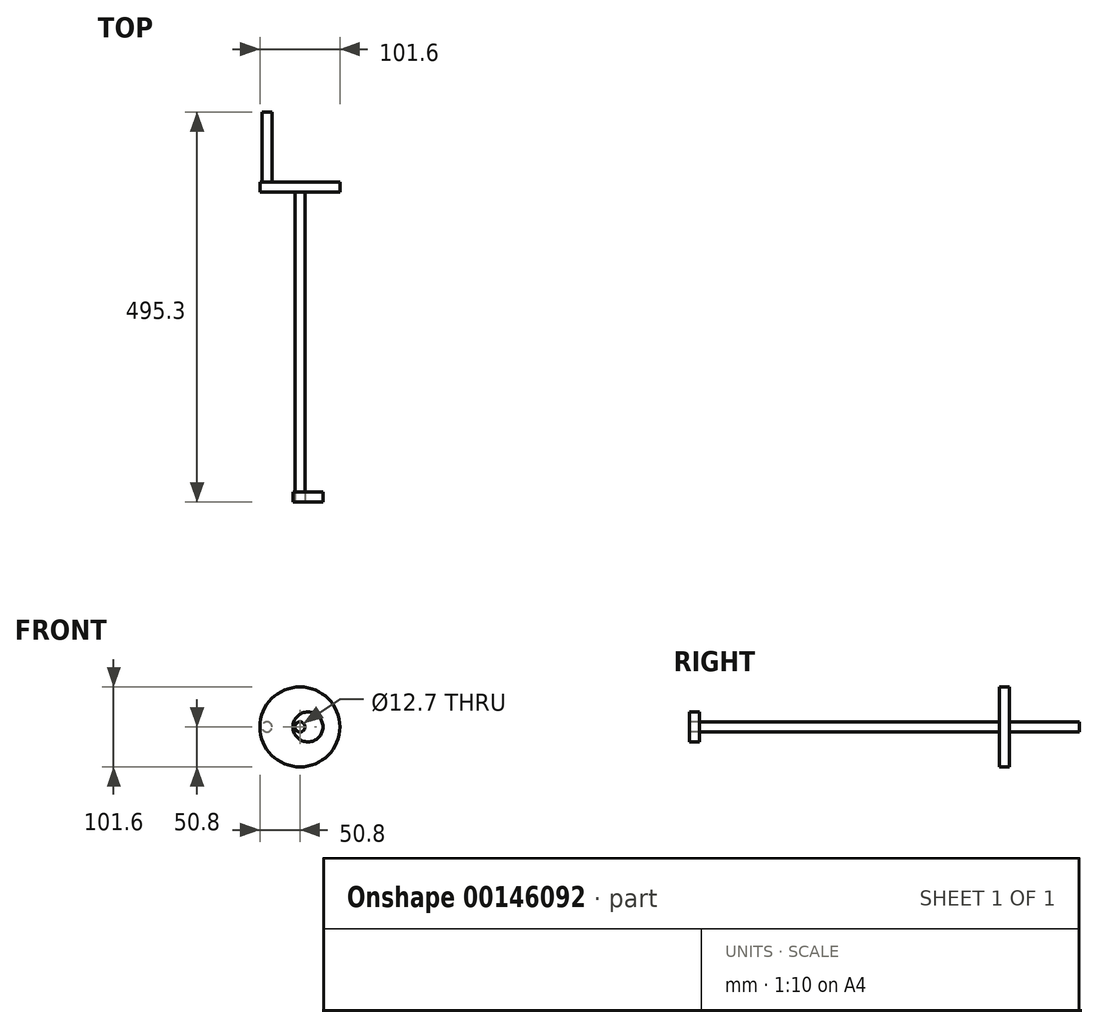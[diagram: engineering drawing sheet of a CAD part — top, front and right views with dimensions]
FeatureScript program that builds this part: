
annotation { "Feature Type Name" : "Feature", "Feature Type Description" : "" }
export const myFeature = defineFeature(function(context is Context, id is Id, definition is map)
    precondition{}
    {
        {
            var Q0;
            Q0=qCreatedBy(makeId("Front.planeOp"),FACE);
            var sketch = newSketch(context, id + "F0", { "sketchPlane" : qUnion([Q0])});
            skCircle(sketch, "E0", {"center": v(0, 0) * mm, "radius": 50.8 * mm});
            skCircle(sketch, "E1", {"center": v(0, 0) * mm, "radius": 6.35 * mm});
            skSolve(sketch);
        }
        {
            var Q0;
            Q0=makeQuery(id+"F0.imprint","IMPRINT",FACE,{"disambiguationData":[TD([[makeQuery(id+"F0.imprint","IMPRINT",EDGE,{"derivedFrom":sQuery(id+"F0.wireOp",EDGE,"E1")}),1.0]])]});
            extrude(context, id + "F1", {"entities" : qUnion([Q0]), "depth" : 393.7 * mm});
        }
        {
            var Q0;
            Q0=makeQuery(id+"F0.imprint","IMPRINT",FACE,{"disambiguationData":[TD([[makeQuery(id+"F0.imprint","IMPRINT",EDGE,{"derivedFrom":sQuery(id+"F0.wireOp",EDGE,"E0")}),1.0]])]});
            extrude(context, id + "F2", {"entities" : qUnion([Q0]), "operationType" : NewBodyOperationType.ADD, "depth" : 12.7 * mm});
        }
        {
            var Q0;
            Q0=makeQuery(id+"F0.imprint","IMPRINT",FACE,{"disambiguationData":[TD([[makeQuery(id+"F0.imprint","IMPRINT",EDGE,{"derivedFrom":sQuery(id+"F0.wireOp",EDGE,"E0")}),1.0]])]});
            var sketch = newSketch(context, id + "F3", { "sketchPlane" : qUnion([Q0])});
            skCircle(sketch, "E2", {"center": v(-41.91, 0) * mm, "radius": 6.35 * mm});
            skSolve(sketch);
        }
        {
            var Q0;
            Q0=makeQuery(id+"F3.imprint","IMPRINT",FACE,{"disambiguationData":[TD([[makeQuery(id+"F3.imprint","IMPRINT",EDGE,{"derivedFrom":sQuery(id+"F3.wireOp",EDGE,"E2")}),1.0]])]});
            extrude(context, id + "F4", {"entities" : qUnion([Q0]), "operationType" : NewBodyOperationType.ADD, "oppositeDirection" : true, "depth" : 88.9 * mm});
        }
        {
            var Q0;
            Q0=qCreatedBy(makeId("Right.planeOp"),FACE);
            var sketch = newSketch(context, id + "F5", { "sketchPlane" : qUnion([Q0])});
            skLineSegment(sketch, "E3", {"start": v(0, 0) * mm, "end": v(-393.7, 0) * mm});
            skLineSegment(sketch, "E4", {"start": v(0, 0) * mm, "end": v(-95.25, 0) * mm});
            skLineSegment(sketch, "E5", {"start": v(-95.25, 0) * mm, "end": v(-260.35, 0) * mm});
            skLineSegment(sketch, "E6", {"start": v(-260.35, 0) * mm, "end": v(-387.35, 0) * mm});
            skLineSegment(sketch, "E7", {"start": v(0, 0) * mm, "end": v(-12.7, 0) * mm});
            skLineSegment(sketch, "E8", {"start": v(-12.7, 0) * mm, "end": v(-19.05, 0) * mm});
            skLineSegment(sketch, "E9", {"start": v(-95.25, 0) * mm, "end": v(-107.95, 0) * mm});
            skLineSegment(sketch, "E10", {"start": v(-107.95, 0) * mm, "end": v(-114.3, 0) * mm});
            skLineSegment(sketch, "E11", {"start": v(-114.3, 0) * mm, "end": v(-127, 0) * mm});
            skLineSegment(sketch, "E12", {"start": v(-127, 0) * mm, "end": v(-133.35, 0) * mm});
            skLineSegment(sketch, "E13.2.0.0", {"start": v(-133.35, 0) * mm, "end": v(-146.05, 0) * mm});
            skLineSegment(sketch, "E13.3.0.0", {"start": v(-152.4, 0) * mm, "end": v(-165.1, 0) * mm});
            skLineSegment(sketch, "E13.4.0.0", {"start": v(-171.45, 0) * mm, "end": v(-184.15, 0) * mm});
            skLineSegment(sketch, "E13.5.0.0", {"start": v(-190.5, 0) * mm, "end": v(-203.2, 0) * mm});
            skLineSegment(sketch, "E13.6.0.0", {"start": v(-209.55, 0) * mm, "end": v(-222.25, 0) * mm});
            skLineSegment(sketch, "E13.7.0.0", {"start": v(-228.6, 0) * mm, "end": v(-241.3, 0) * mm});
            skLineSegment(sketch, "E13.8.0.0", {"start": v(-247.65, 0) * mm, "end": v(-260.35, 0) * mm});
            skLineSegment(sketch, "E13.direction1", {"start": v(-107.95, 0) * mm, "end": v(-127, 0) * mm, "construction": true});
            skSolve(sketch);
        }
        {
            var Q0;
            Q0=sQuery(id+"F5.wireOp",VERTEX,"E3.end");
            var Q1;
            Q1=sQuery(id+"F5.wireOp",EDGE,"E3");
            cPlane(context, id + "F6", {"entities" : qUnion([Q0, Q1]), "cplaneType" : CPlaneType.LINE_POINT, "offset" : 25.4 * mm, "width" : 152.4 * mm, "height" : 152.4 * mm});
        }
        {
            var Q0;
            Q0=qCreatedBy(id+"F6.planeOp",FACE);
            var sketch = newSketch(context, id + "F7", { "sketchPlane" : qUnion([Q0])});
            skPoint(sketch, "E14.0", {"position": v(0, 0) * mm});
            skLineSegment(sketch, "E15", {"start": v(0, 0) * mm, "end": v(10.16, 0) * mm, "construction": true});
            skCircle(sketch, "E16", {"center": v(10.16, 0) * mm, "radius": 19.05 * mm});
            skSolve(sketch);
        }
        {
            var Q0;
            Q0=makeQuery(id+"F7.imprint","IMPRINT",FACE,{"disambiguationData":[TD([[makeQuery(id+"F7.imprint","IMPRINT",EDGE,{"derivedFrom":sQuery(id+"F7.wireOp",EDGE,"E16")}),1.0]])]});
            extrude(context, id + "F8", {"entities" : qUnion([Q0]), "depth" : 12.7 * mm});
        }
        {
            var Q0;
            Q0=makeQuery(id+"F8.opExtrude","CAP_FACE",FACE,{"disambiguationData":[OSD([sQuery(id+"F7.wireOp",EDGE,"E16")])],"isStart":false});
            var sketch = newSketch(context, id + "F9", { "sketchPlane" : qUnion([Q0])});
            skCircle(sketch, "E17", {"center": v(0, 0) * mm, "radius": 6.35 * mm});
            skCircle(sketch, "E18.0", {"center": v(10.16, 0) * mm, "radius": 19.05 * mm});
            skSolve(sketch);
        }
        {
            var Q0;
            Q0=makeQuery(id+"F9.imprint","IMPRINT",FACE,{"disambiguationData":[TD([[makeQuery(id+"F9.imprint","IMPRINT",EDGE,{"derivedFrom":sQuery(id+"F9.wireOp",EDGE,"E17")}),1.0]])]});
            extrude(context, id + "F10", {"entities" : qUnion([Q0]), "operationType" : NewBodyOperationType.REMOVE, "oppositeDirection" : true, "depth" : 12.7 * mm});
        }
        {
            var Q0;
            Q0=sQuery(id+"F5.wireOp",VERTEX,"E9.start");
            var Q1;
            Q1=sQuery(id+"F5.wireOp",EDGE,"E9");
            cPlane(context, id + "F11", {"entities" : qUnion([Q0, Q1]), "cplaneType" : CPlaneType.LINE_POINT, "offset" : 25.4 * mm, "width" : 152.4 * mm, "height" : 152.4 * mm});
        }
    });
